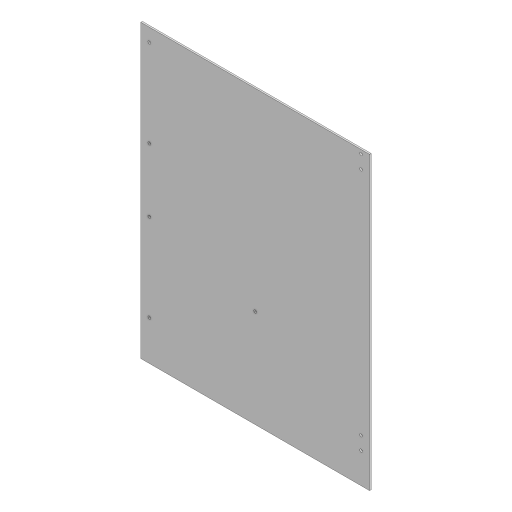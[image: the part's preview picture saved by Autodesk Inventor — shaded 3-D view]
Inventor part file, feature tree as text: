
AUTODESK INVENTOR PART (.ipt)
format: ipt  version: 2023 (Build 270158000, 158)  size: 113,664 bytes
history: native  units: mm
features: sketch x1, extrude x1, hole x1
ambient origin geometry x8: Origin, YZ Plane, XZ Plane, XY Plane, X Axis, Y Axis, Z Axis, Center Point
bodies: Solid1 (feature_tree)
feature tree (3):
  sketch  "Sketch1"  dims[d0=432.0mm d1=550.0mm d2=7.5mm d3=25.0mm d5=25.0mm d7=120.0mm d8=190.0mm d10=500.0mm d11=135.0mm d12=200.0mm d13=25.0mm d14=25.0mm d15=16.0mm d16=16.0mm d17=3.0mm d18=0.0mm d19=5.3mm d20=6.0mm d21=4.0mm d22=2.0mm d23=90.0deg d24=8.0mm d25=20.594885mm d26=7.5mm]
  extrude  "Extrusion1"  Depth=550.0mm
  hole  "Hole1"  [1 undecoded]
note: 1 required parameter value undecoded (feature->parameter linkage not recoverable at this tier; creation-order binding heuristic only, values carry confidence <= 0.55)
